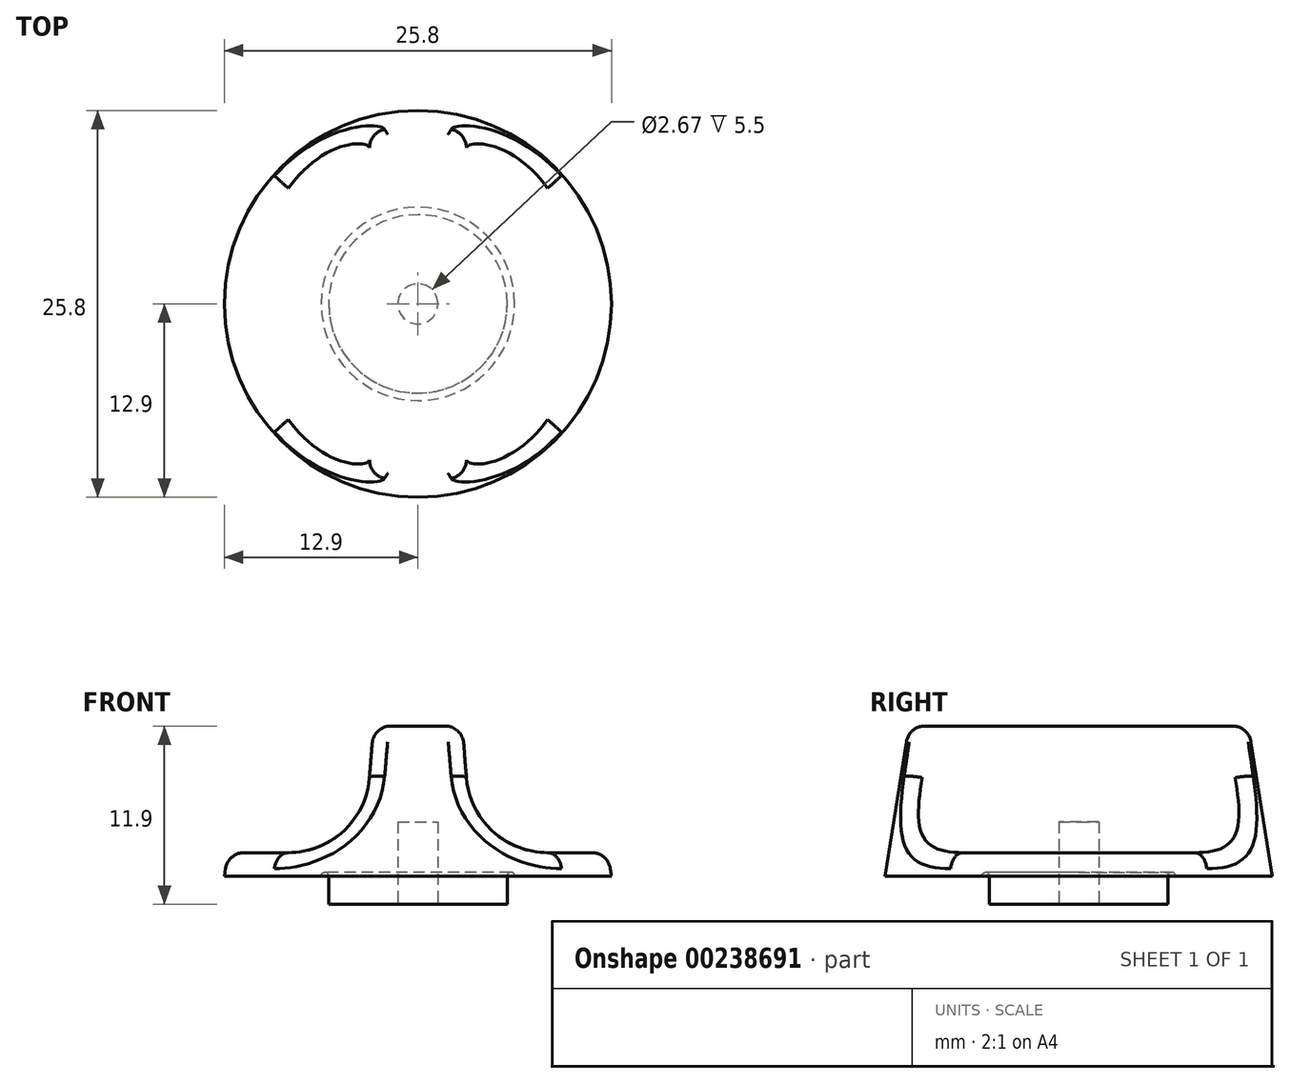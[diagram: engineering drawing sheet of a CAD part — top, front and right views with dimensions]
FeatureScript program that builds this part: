
annotation { "Feature Type Name" : "Feature", "Feature Type Description" : "" }
export const myFeature = defineFeature(function(context is Context, id is Id, definition is map)
    precondition{}
    {
        {
            var Q0;
            Q0=qCreatedBy(makeId("Top.planeOp"),FACE);
            var sketch = newSketch(context, id + "F0", { "sketchPlane" : qUnion([Q0])});
            skCircle(sketch, "E0", {"center": v(0, 0) * mm, "radius": 12.9 * mm});
            skCircle(sketch, "E1", {"center": v(0, 0) * mm, "radius": 5.95 * mm});
            skSolve(sketch);
        }
        {
            var Q0;
            Q0=makeQuery(id+"F0.imprint","IMPRINT",FACE,{"disambiguationData":[TD([[makeQuery(id+"F0.imprint","IMPRINT",EDGE,{"derivedFrom":sQuery(id+"F0.wireOp",EDGE,"E1")}),1.0]])]});
            extrude(context, id + "F1", {"entities" : qUnion([Q0]), "oppositeDirection" : true, "depth" : 1.9 * mm});
        }
        {
            var Q0;
            Q0=makeQuery(id+"F0.imprint","IMPRINT",FACE,{"disambiguationData":[TD([[makeQuery(id+"F0.imprint","IMPRINT",EDGE,{"derivedFrom":sQuery(id+"F0.wireOp",EDGE,"E0")}),1.0]])]});
            var Q1;
            Q1=makeQuery(id+"F0.imprint","IMPRINT",FACE,{"disambiguationData":[TD([[makeQuery(id+"F0.imprint","IMPRINT",EDGE,{"derivedFrom":sQuery(id+"F0.wireOp",EDGE,"E1")}),1.0]])]});
            extrude(context, id + "F2", {"entities" : qUnion([Q0, Q1]), "operationType" : NewBodyOperationType.ADD, "depth" : 10 * mm, "hasDraft" : true, "draftAngle" : 9 * degree, "draftPullDirection" : true});
        }
        {
            var Q0;
            Q0=qCreatedBy(makeId("Front.planeOp"),FACE);
            var sketch = newSketch(context, id + "F3", { "sketchPlane" : qUnion([Q0])});
            skLineSegment(sketch, "E2", {"start": v(2.55, 15.2) * mm, "end": v(3.23, 6.56) * mm});
            skLineSegment(sketch, "E3", {"start": v(8.64, 1.56) * mm, "end": v(19.49, 1.56) * mm});
            skLineSegment(sketch, "E4", {"start": v(19.49, 1.56) * mm, "end": v(19.49, 15.2) * mm});
            skLineSegment(sketch, "E5", {"start": v(19.49, 15.2) * mm, "end": v(2.55, 15.2) * mm});
            skArc(sketch, "E6", {"start": v(3.23, 6.56) * mm, "mid": v(4.96, 3) * mm, "end": v(8.64, 1.56) * mm});
            skLineSegment(sketch, "E7.MirrorCS", {"start": v(-8.64, 1.56) * mm, "end": v(-19.49, 1.56) * mm});
            skLineSegment(sketch, "E8.MirrorCS", {"start": v(-19.49, 1.56) * mm, "end": v(-19.49, 15.2) * mm});
            skLineSegment(sketch, "E9.MirrorCS", {"start": v(-2.55, 15.2) * mm, "end": v(-3.23, 6.56) * mm});
            skLineSegment(sketch, "E10.MirrorCS", {"start": v(-19.49, 15.2) * mm, "end": v(-2.55, 15.2) * mm});
            skArc(sketch, "E11.MirrorCS", {"start": v(-3.23, 6.56) * mm, "mid": v(-4.96, 3) * mm, "end": v(-8.64, 1.56) * mm});
            skSolve(sketch);
        }
        {
            var Q0;
            Q0=makeQuery(id+"F3.imprint","IMPRINT",FACE,{"disambiguationData":[TD([[makeQuery(id+"F3.imprint","IMPRINT",EDGE,{"derivedFrom":sQuery(id+"F3.wireOp",EDGE,"E7.MirrorCS")}),-1.0]])]});
            var Q1;
            Q1=makeQuery(id+"F3.imprint","IMPRINT",FACE,{"disambiguationData":[TD([[makeQuery(id+"F3.imprint","IMPRINT",EDGE,{"derivedFrom":sQuery(id+"F3.wireOp",EDGE,"E2")}),1.0]])]});
            extrude(context, id + "F4", {"entities" : qUnion([Q0, Q1]), "operationType" : NewBodyOperationType.REMOVE, "oppositeDirection" : true, "depth" : 25 * mm, "hasSecondDirection" : true, "secondDirectionOppositeDirection" : false, "secondDirectionDepth" : 25 * mm});
        }
        {
            var Q0;
            Q0=makeQuery(id+"F4.boolean.opBoolean","INTERSECT",EDGE,{"derivedFrom":[makeQuery(id+"F2.opExtrude","CAP_FACE",FACE,{"disambiguationData":[OSD([sQuery(id+"F0.wireOp",EDGE,"E0")])],"isStart":false}),makeQuery(id+"F4.opExtrude","SWEPT_FACE",FACE,{"disambiguationData":[OSD([sQuery(id+"F3.wireOp",EDGE,"E9.MirrorCS")])]})]});
            var Q1;
            Q1=makeQuery(id+"F4.boolean.opBoolean","INTERSECT",EDGE,{"derivedFrom":[makeQuery(id+"F2.opExtrude","CAP_FACE",FACE,{"disambiguationData":[OSD([sQuery(id+"F0.wireOp",EDGE,"E0")])],"isStart":false}),makeQuery(id+"F4.opExtrude","SWEPT_FACE",FACE,{"disambiguationData":[OSD([sQuery(id+"F3.wireOp",EDGE,"E2")])]})]});
            var Q2;
            Q2=makeQuery(id+"F2.opExtrude","CAP_FACE",FACE,{"disambiguationData":[OSD([sQuery(id+"F0.wireOp",EDGE,"E0")])],"isStart":false});
            var Q3;
            Q3=makeQuery(id+"F4.boolean.opBoolean","INTERSECT",EDGE,{"disambiguationData":[OD(1.0)],"derivedFrom":[makeQuery(id+"F2.opExtrude","SWEPT_FACE",FACE,{"disambiguationData":[OSD([sQuery(id+"F0.wireOp",EDGE,"E0")])]}),makeQuery(id+"F4.opExtrude","SWEPT_FACE",FACE,{"disambiguationData":[OSD([sQuery(id+"F3.wireOp",EDGE,"E9.MirrorCS")])]})]});
            var Q4;
            Q4=makeQuery(id+"F4.boolean.opBoolean","INTERSECT",EDGE,{"disambiguationData":[OD(0.0)],"derivedFrom":[makeQuery(id+"F2.opExtrude","SWEPT_FACE",FACE,{"disambiguationData":[OSD([sQuery(id+"F0.wireOp",EDGE,"E0")])]}),makeQuery(id+"F4.opExtrude","SWEPT_FACE",FACE,{"disambiguationData":[OSD([sQuery(id+"F3.wireOp",EDGE,"E6")])]})]});
            fillet(context, id + "F5", {"entities" : qUnion([Q0, Q1, Q2, Q3, Q4]), "radius" : 1.25 * mm, "tangentPropagation" : true, "allowEdgeOverflow" : false});
        }
        {
            var Q0;
            Q0=makeQuery(id+"F1.opExtrude","CAP_FACE",FACE,{"disambiguationData":[OSD([sQuery(id+"F0.wireOp",EDGE,"E1")])],"isStart":false});
            var sketch = newSketch(context, id + "F6", { "sketchPlane" : qUnion([Q0])});
            skCircle(sketch, "E12", {"center": v(0, 0) * mm, "radius": 1.34 * mm});
            skSolve(sketch);
        }
        {
            var Q0;
            Q0=makeQuery(id+"F6.imprint","IMPRINT",FACE,{"disambiguationData":[TD([[makeQuery(id+"F6.imprint","IMPRINT",EDGE,{"derivedFrom":sQuery(id+"F6.wireOp",EDGE,"E12")}),1.0]])]});
            extrude(context, id + "F7", {"entities" : qUnion([Q0]), "operationType" : NewBodyOperationType.REMOVE, "oppositeDirection" : true, "depth" : 5.5 * mm});
        }
        {
            var Q0;
            Q0=qCreatedBy(makeId("Front.planeOp"),FACE);
            var sketch = newSketch(context, id + "F8", { "sketchPlane" : qUnion([Q0])});
            skCircle(sketch, "E13", {"center": v(-6.2, 0) * mm, "radius": 0.25 * mm});
            skSolve(sketch);
        }
        {
            var Q0;
            Q0=makeQuery(id+"F8.imprint","IMPRINT",FACE,{"disambiguationData":[TD([[makeQuery(id+"F8.imprint","IMPRINT",EDGE,{"derivedFrom":sQuery(id+"F8.wireOp",EDGE,"E13")}),1.0]])]});
            var Q1;
            Q1=makeQuery(id+"F1.opExtrude","CAP_EDGE",EDGE,{"disambiguationData":[OSD([sQuery(id+"F0.wireOp",EDGE,"E1")])],"isStart":false});
            revolve(context, id + "F9", {"operationType" : NewBodyOperationType.REMOVE, "entities" : qUnion([Q0]), "axis" : qUnion([Q1]), "revolveType" : RevolveType.FULL, "oppositeDirection" : true});
        }
    });
